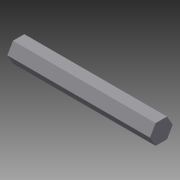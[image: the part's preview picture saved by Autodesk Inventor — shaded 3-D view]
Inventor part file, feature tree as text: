
AUTODESK INVENTOR PART (.ipt)
format: ipt  version: 2015 SP1 (Build 190203100, 203)  size: 77,824 bytes
history: native  units: in
note: dims shown in document units (in); Inventor stores cm internally (conversion verified against a paired STEP export)
features: extrude x1, sketch x1
ambient origin geometry x8: Origin, YZ Plane, XZ Plane, XY Plane, X Axis, Y Axis, Z Axis, Center Point
bodies: Solid1 (feature_tree)
feature tree (2):
  extrude  "Extrusion1"  Depth=0.5in
  sketch  "Sketch1"  dims[d0=0.5in d1=0.5in d2=0.5in d3=0.25in d4=120.0deg d5=120.0deg d6=0.25in d7=0.25in d8=3.625in d9=0.0in]
